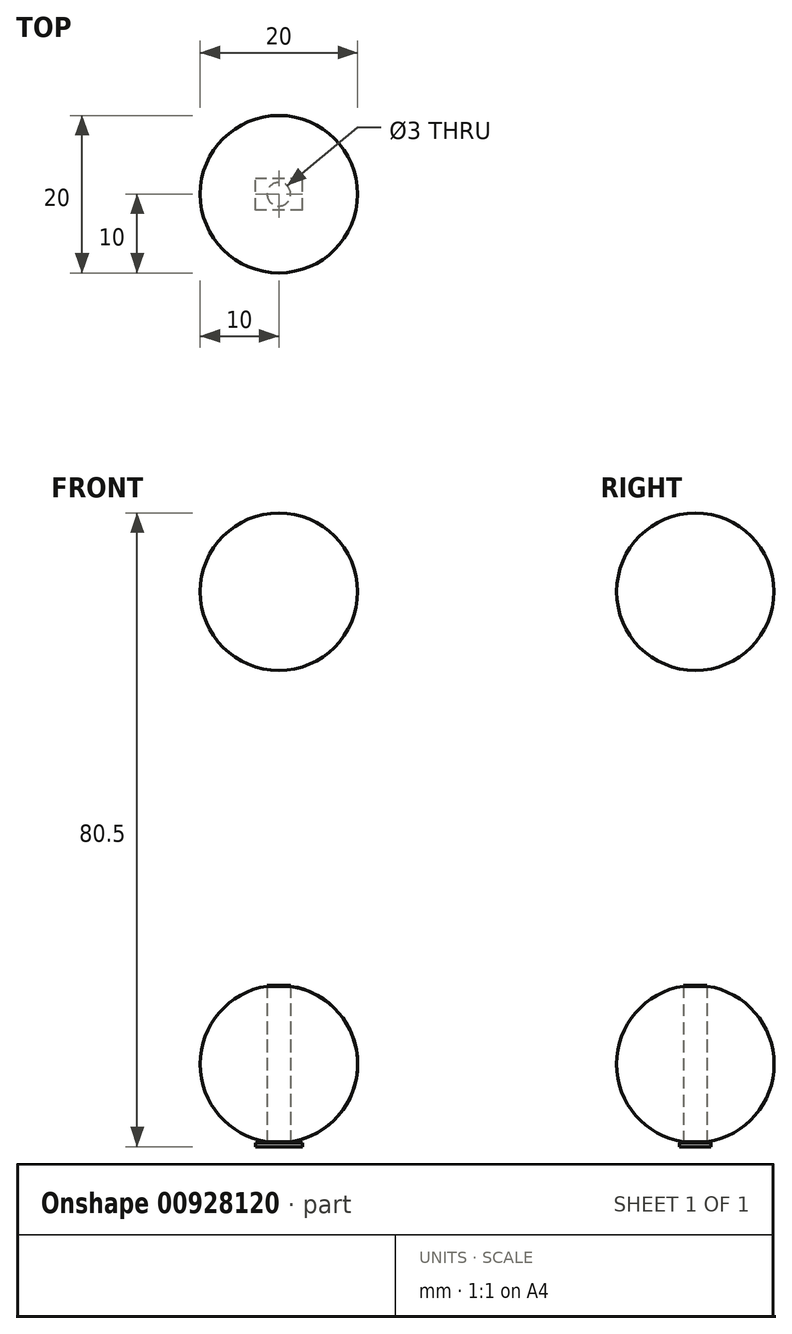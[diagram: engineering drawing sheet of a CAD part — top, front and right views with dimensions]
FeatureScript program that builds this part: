
annotation { "Feature Type Name" : "Feature", "Feature Type Description" : "" }
export const myFeature = defineFeature(function(context is Context, id is Id, definition is map)
    precondition{}
    {
        {
            var Q0;
            Q0=qCreatedBy(makeId("Front.planeOp"),FACE);
            var sketch = newSketch(context, id + "F0", { "sketchPlane" : qUnion([Q0])});
            skLineSegment(sketch, "E0", {"start": v(0, 0) * mm, "end": v(0, 20) * mm});
            skArc(sketch, "E1", {"start": v(0, 20) * mm, "mid": v(10, 10) * mm, "end": v(0, 0) * mm});
            skLineSegment(sketch, "E2.0.1.0", {"start": v(0, 60) * mm, "end": v(0, 80) * mm});
            skArc(sketch, "E2.0.1.1", {"start": v(0, 80) * mm, "mid": v(10, 70) * mm, "end": v(0, 60) * mm});
            skLineSegment(sketch, "E2.direction1", {"start": v(0, 0) * mm, "end": v(25, 0) * mm, "construction": true});
            skLineSegment(sketch, "E2.direction2", {"start": v(0, 0) * mm, "end": v(0, 60) * mm, "construction": true});
            skSolve(sketch);
        }
        {
            var Q0;
            Q0 = qSketchRegion(id + "F0", true);
            var Q1;
            Q1=sQuery(id+"F0.wireOp",EDGE,"E0");
            revolve(context, id + "F1", {"surfaceOperationType" : NewSurfaceOperationType.NEW, "entities" : qUnion([Q0]), "axis" : qUnion([Q1]), "revolveType" : RevolveType.FULL});
        }
        {
            var Q0;
            Q0=qCreatedBy(makeId("Top.planeOp"),FACE);
            var sketch = newSketch(context, id + "F2", { "sketchPlane" : qUnion([Q0])});
            skCircle(sketch, "E3", {"center": v(0, 0) * mm, "radius": 1.5 * mm});
            skSolve(sketch);
        }
        {
            var Q0;
            Q0 = qSketchRegion(id + "F2", true);
            extrude(context, id + "F3", {"entities" : qUnion([Q0]), "depth" : 20 * mm, "offsetDistance" : 25 * mm});
        }
        {
            var Q0;
            Q0=makeQuery(id+"F3.opExtrude","SWEPT_BODY",BODY,{"disambiguationData":[OSD([sQuery(id+"F2.wireOp",EDGE,"E3")])]});
            var Q1;
            Q1=makeQuery(id+"F1.opRevolve","SWEPT_BODY",BODY,{"disambiguationData":[OSD([sQuery(id+"F0.wireOp",EDGE,"E0"),sQuery(id+"F0.wireOp",EDGE,"E1")])]});
            booleanBodies(context, id + "F4", {"operationType" : BooleanOperationType.SUBTRACTION, "tools" : qUnion([Q0]), "targets" : qUnion([Q1]), "keepTools" : true});
        }
        {
            var Q0;
            Q0=qCreatedBy(makeId("Top.planeOp"),FACE);
            var sketch = newSketch(context, id + "F5", { "sketchPlane" : qUnion([Q0])});
            skLineSegment(sketch, "E4.bottom", {"start": v(3, -2) * mm, "end": v(-3, -2) * mm});
            skLineSegment(sketch, "E4.top", {"start": v(3, 2) * mm, "end": v(-3, 2) * mm});
            skLineSegment(sketch, "E4.left", {"start": v(3, -2) * mm, "end": v(3, 2) * mm});
            skLineSegment(sketch, "E4.right", {"start": v(-3, -2) * mm, "end": v(-3, 2) * mm});
            skPoint(sketch, "E4.middle", {"position": v(0, 0) * mm});
            skSolve(sketch);
        }
        {
            var Q0;
            Q0 = qSketchRegion(id + "F5", true);
            extrude(context, id + "F6", {"entities" : qUnion([Q0]), "oppositeDirection" : true, "depth" : 0.5 * mm, "offsetDistance" : 25 * mm});
        }
    });
